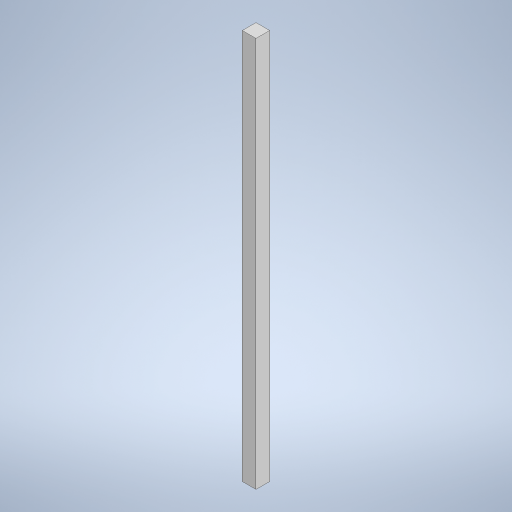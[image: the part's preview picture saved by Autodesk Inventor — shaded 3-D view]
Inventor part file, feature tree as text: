
AUTODESK INVENTOR PART (.ipt)
format: ipt  version: 2023 (Build 270158000, 158)  size: 231,936 bytes
history: native  units: mm
features: other x1, extrude x1, sketch x1
ambient origin geometry x8: Origin, YZ Plane, XZ Plane, XY Plane, X Axis, Y Axis, Z Axis, Center Point
bodies: Body1 (feature_tree)
feature tree (3):
  other  "ソリッド1"
  extrude  "押し出し1"  Depth=10.0mm
  sketch  "スケッチ1"
